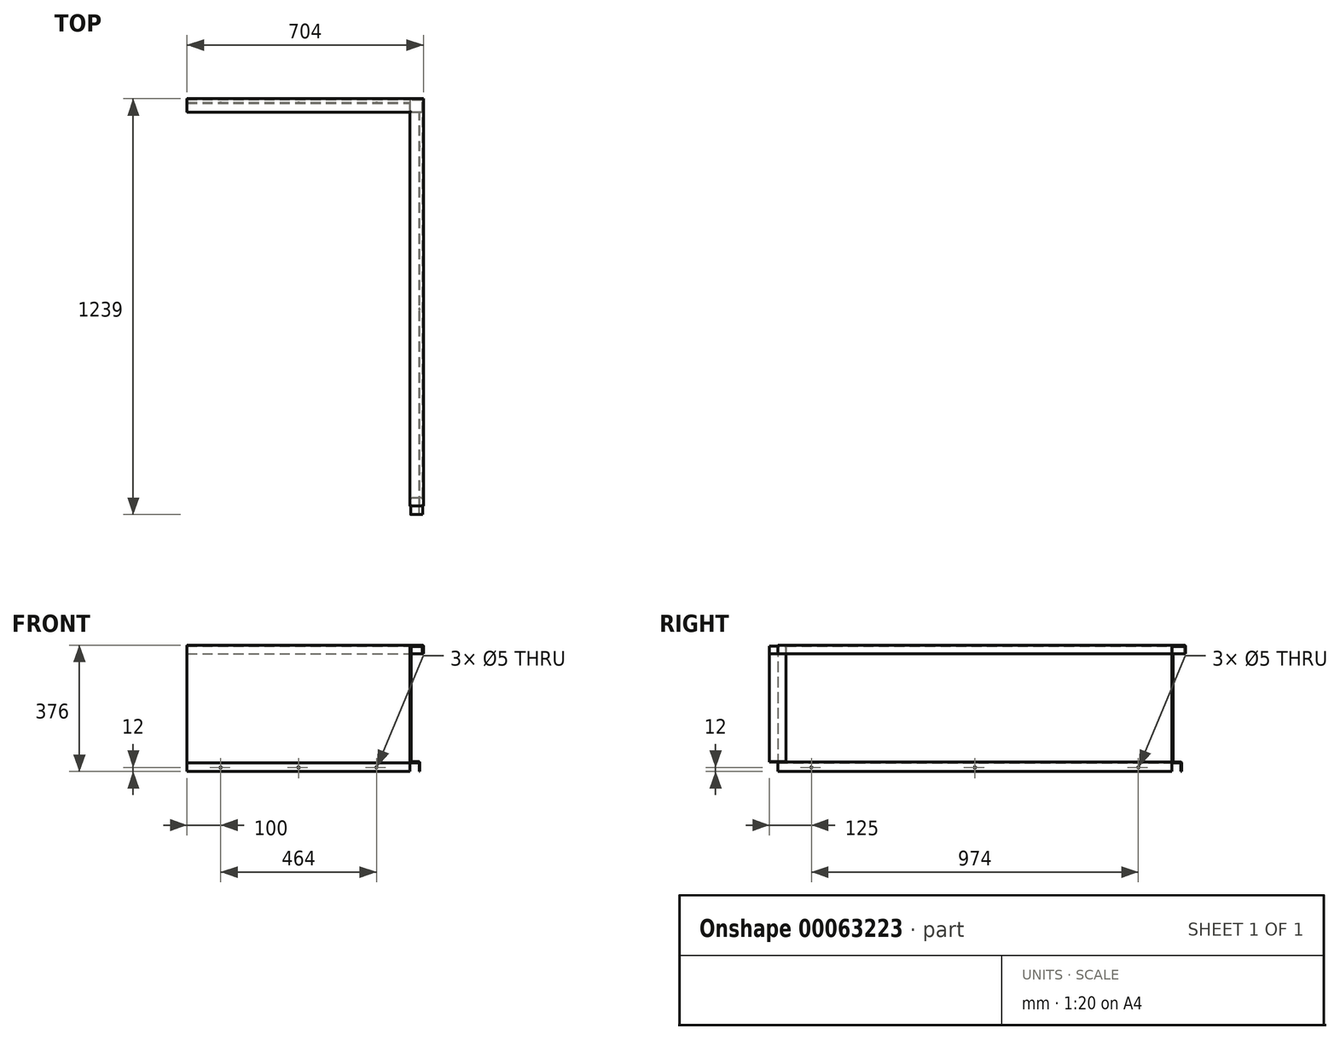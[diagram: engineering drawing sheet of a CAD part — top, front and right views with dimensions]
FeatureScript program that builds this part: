
annotation { "Feature Type Name" : "Feature", "Feature Type Description" : "" }
export const myFeature = defineFeature(function(context is Context, id is Id, definition is map)
    precondition{}
    {
        {
            var Q0;
            Q0=qCreatedBy(makeId("Front.planeOp"),FACE);
            var sketch = newSketch(context, id + "F0", { "sketchPlane" : qUnion([Q0])});
            skLineSegment(sketch, "E0", {"start": v(38, -25) * mm, "end": v(38, -2) * mm});
            skLineSegment(sketch, "E1", {"start": v(38, -2) * mm, "end": v(2, -2) * mm});
            skLineSegment(sketch, "E2", {"start": v(2, -2) * mm, "end": v(2, -348) * mm});
            skLineSegment(sketch, "E3", {"start": v(2, -348) * mm, "end": v(29, -348) * mm});
            skLineSegment(sketch, "E4", {"start": v(29, -348) * mm, "end": v(29, -376) * mm});
            skLineSegment(sketch, "E5.0", {"start": v(27, -350) * mm, "end": v(27, -376) * mm});
            skLineSegment(sketch, "E5.1", {"start": v(40, -25) * mm, "end": v(40, 0) * mm});
            skLineSegment(sketch, "E5.2", {"start": v(40, 0) * mm, "end": v(0, 0) * mm});
            skLineSegment(sketch, "E5.3", {"start": v(0, 0) * mm, "end": v(0, -350) * mm});
            skLineSegment(sketch, "E5.4", {"start": v(0, -350) * mm, "end": v(27, -350) * mm});
            skLineSegment(sketch, "E6", {"start": v(27, -376) * mm, "end": v(29, -376) * mm});
            skLineSegment(sketch, "E7", {"start": v(38, -25) * mm, "end": v(40, -25) * mm});
            skSolve(sketch);
        }
        {
            var Q0;
            Q0=qSketchRegion(id+"F0",true);
            extrude(context, id + "F1", {"entities" : qUnion([Q0]), "depth" : 1174 * mm});
        }
        {
            var Q0;
            Q0=qCreatedBy(makeId("Right.planeOp"),FACE);
            var sketch = newSketch(context, id + "F2", { "sketchPlane" : qUnion([Q0])});
            skLineSegment(sketch, "E8", {"start": v(38, -25) * mm, "end": v(38, -2) * mm});
            skLineSegment(sketch, "E9", {"start": v(38, -2) * mm, "end": v(2, -2) * mm});
            skLineSegment(sketch, "E10", {"start": v(2, -2) * mm, "end": v(2, -348) * mm});
            skLineSegment(sketch, "E11", {"start": v(2, -348) * mm, "end": v(29, -348) * mm});
            skLineSegment(sketch, "E12", {"start": v(29, -348) * mm, "end": v(29, -376) * mm});
            skLineSegment(sketch, "E13.0", {"start": v(27, -350) * mm, "end": v(27, -376) * mm});
            skLineSegment(sketch, "E13.1", {"start": v(40, -25) * mm, "end": v(40, 0) * mm});
            skLineSegment(sketch, "E13.2", {"start": v(40, 0) * mm, "end": v(0, 0) * mm});
            skLineSegment(sketch, "E13.3", {"start": v(0, 0) * mm, "end": v(0, -350) * mm});
            skLineSegment(sketch, "E13.4", {"start": v(0, -350) * mm, "end": v(27, -350) * mm});
            skLineSegment(sketch, "E14", {"start": v(27, -376) * mm, "end": v(29, -376) * mm});
            skLineSegment(sketch, "E15", {"start": v(38, -25) * mm, "end": v(40, -25) * mm});
            skSolve(sketch);
        }
        {
            var Q0;
            Q0=qSketchRegion(id+"F2",true);
            extrude(context, id + "F3", {"entities" : qUnion([Q0]), "oppositeDirection" : true, "depth" : 664 * mm});
        }
        {
            var Q0;
            Q0=qCreatedBy(makeId("Top.planeOp"),FACE);
            var sketch = newSketch(context, id + "F4", { "sketchPlane" : qUnion([Q0])});
            skLineSegment(sketch, "E16", {"start": v(40, 0) * mm, "end": v(40, 40) * mm});
            skLineSegment(sketch, "E17", {"start": v(40, 40) * mm, "end": v(0, 40) * mm});
            skLineSegment(sketch, "E18", {"start": v(0, 40) * mm, "end": v(0, 0) * mm});
            skLineSegment(sketch, "E19", {"start": v(0, 0) * mm, "end": v(40, 0) * mm});
            skSolve(sketch);
        }
        {
            var Q0;
            Q0=qSketchRegion(id+"F4",true);
            extrude(context, id + "F5", {"entities" : qUnion([Q0]), "oppositeDirection" : true, "depth" : 4 * mm});
        }
        {
            var Q0;
            Q0=qCreatedBy(makeId("Top.planeOp"),FACE);
            var sketch = newSketch(context, id + "F6", { "sketchPlane" : qUnion([Q0])});
            skLineSegment(sketch, "E20", {"start": v(0, 0) * mm, "end": v(4, 0) * mm});
            skLineSegment(sketch, "E21", {"start": v(4, 0) * mm, "end": v(4, 4) * mm});
            skLineSegment(sketch, "E22", {"start": v(4, 4) * mm, "end": v(0, 4) * mm});
            skLineSegment(sketch, "E23", {"start": v(0, 4) * mm, "end": v(0, 0) * mm});
            skSolve(sketch);
        }
        {
            var Q0;
            Q0=qSketchRegion(id+"F6",true);
            extrude(context, id + "F7", {"entities" : qUnion([Q0]), "operationType" : NewBodyOperationType.ADD, "oppositeDirection" : true, "depth" : 350 * mm});
        }
        {
            var Q0;
            Q0=makeQuery(id+"F1.opExtrude","SWEPT_EDGE",EDGE,{"disambiguationData":[OSD([sQuery(id+"F0.wireOp",EDGE,"E5.1"),sQuery(id+"F0.wireOp",EDGE,"E5.2")])]});
            var Q1;
            Q1=makeQuery(id+"F3.opExtrude","SWEPT_EDGE",EDGE,{"disambiguationData":[OSD([sQuery(id+"F2.wireOp",EDGE,"E13.1"),sQuery(id+"F2.wireOp",EDGE,"E13.2")])]});
            var Q2;
            Q2=makeQuery(id+"F7.opExtrude","SWEPT_EDGE",EDGE,{"disambiguationData":[OSD([sQuery(id+"F6.wireOp",EDGE,"E21"),sQuery(id+"F6.wireOp",EDGE,"E22")])]});
            var Q3;
            Q3=makeQuery(id+"F3.opExtrude","SWEPT_EDGE",EDGE,{"disambiguationData":[OSD([sQuery(id+"F2.wireOp",EDGE,"E11"),sQuery(id+"F2.wireOp",EDGE,"E12")])]});
            var Q4;
            Q4=makeQuery(id+"F1.opExtrude","SWEPT_EDGE",EDGE,{"disambiguationData":[OSD([sQuery(id+"F0.wireOp",EDGE,"E3"),sQuery(id+"F0.wireOp",EDGE,"E4")])]});
            var Q5;
            Q5=makeQuery(id+"F1.opExtrude","SWEPT_EDGE",EDGE,{"disambiguationData":[OSD([sQuery(id+"F0.wireOp",EDGE,"E2"),sQuery(id+"F0.wireOp",EDGE,"E3")])]});
            var Q6;
            Q6=makeQuery(id+"F3.opExtrude","SWEPT_EDGE",EDGE,{"disambiguationData":[OSD([sQuery(id+"F2.wireOp",EDGE,"E10"),sQuery(id+"F2.wireOp",EDGE,"E11")])]});
            var Q7;
            Q7=makeQuery(id+"F1.opExtrude","SWEPT_EDGE",EDGE,{"disambiguationData":[OSD([sQuery(id+"F0.wireOp",EDGE,"E5.2"),sQuery(id+"F0.wireOp",EDGE,"E5.3")])]});
            var Q8;
            Q8=makeQuery(id+"F3.opExtrude","SWEPT_EDGE",EDGE,{"disambiguationData":[OSD([sQuery(id+"F2.wireOp",EDGE,"E13.2"),sQuery(id+"F2.wireOp",EDGE,"E13.3")])]});
            var Q9;
            Q9=makeQuery(id+"F1.opExtrude","SWEPT_EDGE",EDGE,{"disambiguationData":[OSD([sQuery(id+"F0.wireOp",EDGE,"E1"),sQuery(id+"F0.wireOp",EDGE,"E2")])]});
            var Q10;
            Q10=makeQuery(id+"F3.opExtrude","SWEPT_EDGE",EDGE,{"disambiguationData":[OSD([sQuery(id+"F2.wireOp",EDGE,"E9"),sQuery(id+"F2.wireOp",EDGE,"E10")])]});
            var Q11;
            Q11=makeQuery(id+"F1.opExtrude","SWEPT_EDGE",EDGE,{"disambiguationData":[OSD([sQuery(id+"F0.wireOp",EDGE,"E0"),sQuery(id+"F0.wireOp",EDGE,"E1")])]});
            var Q12;
            Q12=makeQuery(id+"F3.opExtrude","SWEPT_EDGE",EDGE,{"disambiguationData":[OSD([sQuery(id+"F2.wireOp",EDGE,"E8"),sQuery(id+"F2.wireOp",EDGE,"E9")])]});
            var Q13;
            Q13=makeQuery(id+"F3.opExtrude","SWEPT_EDGE",EDGE,{"disambiguationData":[OSD([sQuery(id+"F2.wireOp",EDGE,"E13.3"),sQuery(id+"F2.wireOp",EDGE,"E13.4")])]});
            var Q14;
            Q14=makeQuery(id+"F3.opExtrude","SWEPT_EDGE",EDGE,{"disambiguationData":[OSD([sQuery(id+"F2.wireOp",EDGE,"E13.0"),sQuery(id+"F2.wireOp",EDGE,"E13.4")])]});
            var Q15;
            Q15=makeQuery(id+"F1.opExtrude","SWEPT_EDGE",EDGE,{"disambiguationData":[OSD([sQuery(id+"F0.wireOp",EDGE,"E5.3"),sQuery(id+"F0.wireOp",EDGE,"E5.4")])]});
            var Q16;
            Q16=makeQuery(id+"F1.opExtrude","SWEPT_EDGE",EDGE,{"disambiguationData":[OSD([sQuery(id+"F0.wireOp",EDGE,"E5.0"),sQuery(id+"F0.wireOp",EDGE,"E5.4")])]});
            var Q17;
            Q17=makeQuery(id+"F5.opExtrude","CAP_EDGE",EDGE,{"disambiguationData":[OSD([sQuery(id+"F4.wireOp",EDGE,"E16")])],"isStart":true});
            var Q18;
            Q18=makeQuery(id+"F5.opExtrude","CAP_EDGE",EDGE,{"disambiguationData":[OSD([sQuery(id+"F4.wireOp",EDGE,"E17")])],"isStart":true});
            fillet(context, id + "F8", {"entities" : qUnion([Q0, Q1, Q2, Q3, Q4, Q5, Q6, Q7, Q8, Q9, Q10, Q11, Q12, Q13, Q14, Q15, Q16, Q17, Q18]), "radius" : 2 * mm, "tangentPropagation" : true, "allowEdgeOverflow" : false});
        }
        {
            var Q0;
            Q0=makeQuery(id+"F5.opExtrude","CAP_FACE",FACE,{"disambiguationData":[OSD([sQuery(id+"F4.wireOp",EDGE,"E16"),sQuery(id+"F4.wireOp",EDGE,"E17"),sQuery(id+"F4.wireOp",EDGE,"E18"),sQuery(id+"F4.wireOp",EDGE,"E19")])],"isStart":false});
            var sketch = newSketch(context, id + "F9", { "sketchPlane" : qUnion([Q0])});
            skLineSegment(sketch, "E24", {"start": v(40, 0) * mm, "end": v(40, -40) * mm});
            skLineSegment(sketch, "E25", {"start": v(40, -40) * mm, "end": v(0, -40) * mm});
            skLineSegment(sketch, "E26.0", {"start": v(36, -36) * mm, "end": v(0, -36) * mm});
            skLineSegment(sketch, "E26.1", {"start": v(36, 0) * mm, "end": v(36, -36) * mm});
            skLineSegment(sketch, "E27", {"start": v(36, 0) * mm, "end": v(40, 0) * mm});
            skLineSegment(sketch, "E28", {"start": v(0, -36) * mm, "end": v(0, -40) * mm});
            skSolve(sketch);
        }
        {
            var Q0;
            Q0=qSketchRegion(id+"F9",true);
            extrude(context, id + "F10", {"entities" : qUnion([Q0]), "depth" : 21 * mm});
        }
        {
            var Q0;
            Q0=makeQuery(id+"F1.opExtrude","CAP_FACE",FACE,{"disambiguationData":[OSD([sQuery(id+"F0.wireOp",EDGE,"E0"),sQuery(id+"F0.wireOp",EDGE,"E1"),sQuery(id+"F0.wireOp",EDGE,"E2"),sQuery(id+"F0.wireOp",EDGE,"E3"),sQuery(id+"F0.wireOp",EDGE,"E4"),sQuery(id+"F0.wireOp",EDGE,"E5.0"),sQuery(id+"F0.wireOp",EDGE,"E5.1"),sQuery(id+"F0.wireOp",EDGE,"E5.2"),sQuery(id+"F0.wireOp",EDGE,"E5.3"),sQuery(id+"F0.wireOp",EDGE,"E5.4"),sQuery(id+"F0.wireOp",EDGE,"E6"),sQuery(id+"F0.wireOp",EDGE,"E7")])],"isStart":false});
            var sketch = newSketch(context, id + "F11", { "sketchPlane" : qUnion([Q0])});
            skLineSegment(sketch, "E29.0", {"start": v(4, -346) * mm, "end": v(27, -346) * mm});
            skLineSegment(sketch, "E29.1", {"start": v(4, -4) * mm, "end": v(4, -346) * mm});
            skLineSegment(sketch, "E29.2", {"start": v(36, -4) * mm, "end": v(4, -4) * mm});
            skLineSegment(sketch, "E29.3", {"start": v(36, -25) * mm, "end": v(36, -4) * mm});
            skLineSegment(sketch, "E30.0", {"start": v(38, -25) * mm, "end": v(38, -4) * mm});
            skArc(sketch, "E31.0", {"start": v(36, -2) * mm, "mid": v(37.41, -2.59) * mm, "end": v(38, -4) * mm});
            skLineSegment(sketch, "E32.0", {"start": v(36, -2) * mm, "end": v(4, -2) * mm});
            skArc(sketch, "E33.0", {"start": v(2, -4) * mm, "mid": v(2.59, -2.59) * mm, "end": v(4, -2) * mm});
            skLineSegment(sketch, "E34.0", {"start": v(2, -4) * mm, "end": v(2, -346) * mm});
            skLineSegment(sketch, "E35.0", {"start": v(4, -348) * mm, "end": v(27, -348) * mm});
            skArc(sketch, "E36.0", {"start": v(4, -348) * mm, "mid": v(2.59, -347.41) * mm, "end": v(2, -346) * mm});
            skLineSegment(sketch, "E37", {"start": v(27, -346) * mm, "end": v(27, -348) * mm});
            skLineSegment(sketch, "E38", {"start": v(38, -25) * mm, "end": v(36, -25) * mm});
            skSolve(sketch);
        }
        {
            var Q0;
            Q0=qSketchRegion(id+"F11",true);
            extrude(context, id + "F12", {"entities" : qUnion([Q0]), "operationType" : NewBodyOperationType.ADD, "depth" : 25 * mm, "hasSecondDirection" : true, "secondDirectionOppositeDirection" : true, "secondDirectionDepth" : 25 * mm});
        }
        {
            var Q0;
            Q0=makeQuery(id+"F3.opExtrude","SWEPT_FACE",FACE,{"disambiguationData":[OSD([sQuery(id+"F2.wireOp",EDGE,"E13.0")])]});
            var sketch = newSketch(context, id + "F13", { "sketchPlane" : qUnion([Q0])});
            skLineSegment(sketch, "E39", {"start": v(-664, -364) * mm, "end": v(0, -364) * mm, "construction": true});
            skPoint(sketch, "E40", {"position": v(-564, -364) * mm});
            skPoint(sketch, "E41", {"position": v(-332, -364) * mm});
            skPoint(sketch, "E42", {"position": v(-100, -364) * mm});
            skSolve(sketch);
        }
        {
            var Q0;
            Q0=makeQuery(id+"F1.opExtrude","SWEPT_FACE",FACE,{"disambiguationData":[OSD([sQuery(id+"F0.wireOp",EDGE,"E5.0")])]});
            var sketch = newSketch(context, id + "F14", { "sketchPlane" : qUnion([Q0])});
            skPoint(sketch, "E43", {"position": v(1074, -364) * mm});
            skPoint(sketch, "E44", {"position": v(587, -364) * mm});
            skPoint(sketch, "E45", {"position": v(100, -364) * mm});
            skLineSegment(sketch, "E46", {"start": v(0, -364) * mm, "end": v(1174, -364) * mm, "construction": true});
            skSolve(sketch);
        }
        {
            var Q0;
            Q0=sQuery(id+"F14.wireOp",VERTEX,"E45");
            var Q1;
            Q1=sQuery(id+"F14.wireOp",VERTEX,"E44");
            var Q2;
            Q2=sQuery(id+"F14.wireOp",VERTEX,"E43");
            var Q3;
            Q3=sQuery(id+"F13.wireOp",VERTEX,"E42");
            var Q4;
            Q4=sQuery(id+"F13.wireOp",VERTEX,"E41");
            var Q5;
            Q5=sQuery(id+"F13.wireOp",VERTEX,"E40");
            var Q6;
            Q6=makeQuery(id+"F1.opExtrude","SWEPT_BODY",BODY,{"disambiguationData":[OSD([sQuery(id+"F0.wireOp",EDGE,"E0"),sQuery(id+"F0.wireOp",EDGE,"E1"),sQuery(id+"F0.wireOp",EDGE,"E2"),sQuery(id+"F0.wireOp",EDGE,"E3"),sQuery(id+"F0.wireOp",EDGE,"E4"),sQuery(id+"F0.wireOp",EDGE,"E5.0"),sQuery(id+"F0.wireOp",EDGE,"E5.1"),sQuery(id+"F0.wireOp",EDGE,"E5.2"),sQuery(id+"F0.wireOp",EDGE,"E5.3"),sQuery(id+"F0.wireOp",EDGE,"E5.4"),sQuery(id+"F0.wireOp",EDGE,"E6"),sQuery(id+"F0.wireOp",EDGE,"E7")])]});
            hole(context, id + "F15", {"style" : HoleStyle.SIMPLE, "holeDiameter" : 5 * mm, "endStyle" : HoleEndStyle.THROUGH, "locations" : qUnion([Q0, Q1, Q2, Q3, Q4, Q5]), "scope" : qUnion([Q6])});
        }
    });
